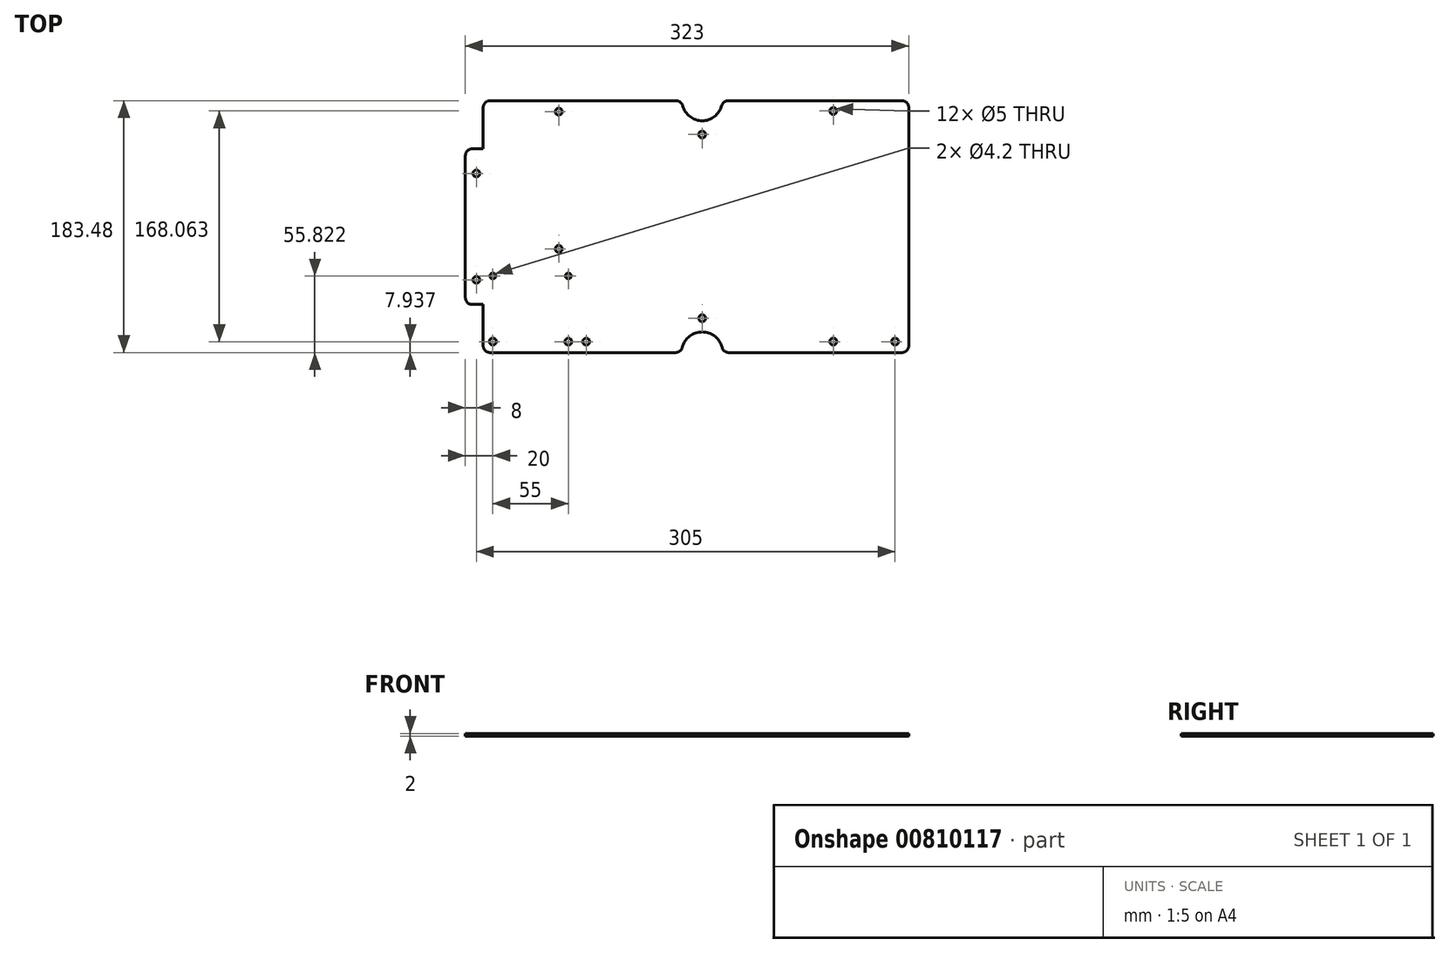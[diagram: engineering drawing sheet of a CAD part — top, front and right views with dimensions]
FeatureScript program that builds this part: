
annotation { "Feature Type Name" : "Feature", "Feature Type Description" : "" }
export const myFeature = defineFeature(function(context is Context, id is Id, definition is map)
    precondition{}
    {
        {
            var Q0;
            Q0=qCreatedBy(makeId("Top.planeOp"),FACE);
            var sketch = newSketch(context, id + "F0", { "sketchPlane" : qUnion([Q0])});
            skLineSegment(sketch, "E0.bottom", {"start": v(-154.5, 90.98) * mm, "end": v(-19, 90.98) * mm});
            skLineSegment(sketch, "E0.top", {"start": v(-154.5, -92.5) * mm, "end": v(-19.36, -92.5) * mm});
            skLineSegment(sketch, "E0.left", {"start": v(-172.5, 50.98) * mm, "end": v(-172.5, -52.5) * mm});
            skLineSegment(sketch, "E0.right", {"start": v(150.5, 85.98) * mm, "end": v(150.5, -87.5) * mm});
            skPoint(sketch, "E0.middle", {"position": v(0, 0) * mm});
            skArc(sketch, "E1.filletArc", {"start": v(145.5, -92.5) * mm, "mid": v(149.04, -91.04) * mm, "end": v(150.5, -87.5) * mm});
            skArc(sketch, "E2.filletArc", {"start": v(150.5, 85.98) * mm, "mid": v(149.04, 89.51) * mm, "end": v(145.5, 90.98) * mm});
            skPoint(sketch, "E3", {"position": v(-104.5, 82.98) * mm});
            skPoint(sketch, "E4.endSnap0", {"position": v(0, 90.98) * mm});
            skPoint(sketch, "E5.endSnap0", {"position": v(-172.5, -0.76) * mm});
            skPoint(sketch, "E6.MirrorP", {"position": v(95.5, 83.5) * mm});
            skPoint(sketch, "E7.MirrorP", {"position": v(162.5, 84.5) * mm});
            skPoint(sketch, "E8.MirrorP", {"position": v(140.5, -84.5) * mm});
            skPoint(sketch, "E9.MirrorP", {"position": v(95.5, -84.5) * mm});
            skPoint(sketch, "E10.MirrorP", {"position": v(-152.5, -84.5) * mm});
            skPoint(sketch, "E11.MirrorP", {"position": v(-97.5, -84.56) * mm});
            skPoint(sketch, "E12", {"position": v(-97.5, -36.68) * mm});
            skPoint(sketch, "E13", {"position": v(-152.5, -36.68) * mm});
            skLineSegment(sketch, "E14.bottom", {"start": v(-167.5, -57.5) * mm, "end": v(-159.5, -57.5) * mm});
            skLineSegment(sketch, "E14.right", {"start": v(-159.5, -57.5) * mm, "end": v(-159.5, -87.5) * mm});
            skPoint(sketch, "E14.left.start.orphan", {"position": v(-172.5, -87.5) * mm});
            skLineSegment(sketch, "E15.bottom", {"start": v(-167.5, 55.98) * mm, "end": v(-159.5, 55.98) * mm});
            skLineSegment(sketch, "E15.right", {"start": v(-159.5, 55.98) * mm, "end": v(-159.5, 85.98) * mm});
            skPoint(sketch, "E16.filletArc.end.orphan", {"position": v(-172.5, 85.98) * mm});
            skPoint(sketch, "E15.top.end.orphan", {"position": v(-145.5, 90.98) * mm});
            skArc(sketch, "E17", {"start": v(-14.17, 87.25) * mm, "mid": v(0, 76.33) * mm, "end": v(14.17, 87.25) * mm});
            skArc(sketch, "E18", {"start": v(14.52, -88.75) * mm, "mid": v(0, -77.5) * mm, "end": v(-14.52, -88.75) * mm});
            skPoint(sketch, "E18.centerSnap0", {"position": v(-7, -92.5) * mm});
            skLineSegment(sketch, "E19.trimOffspring", {"start": v(19, 90.98) * mm, "end": v(145.5, 90.98) * mm});
            skLineSegment(sketch, "E20.trimOffspring", {"start": v(-7, -92.5) * mm, "end": v(0, -92.5) * mm});
            skLineSegment(sketch, "E21.trimOffspring", {"start": v(19.36, -92.5) * mm, "end": v(145.5, -92.5) * mm});
            skPoint(sketch, "E22.visualSharp", {"position": v(14.65, 90.98) * mm});
            skArc(sketch, "E22.filletArc", {"start": v(19, 90.98) * mm, "mid": v(15.95, 89.94) * mm, "end": v(14.17, 87.25) * mm});
            skPoint(sketch, "E23.visualSharp", {"position": v(-14.65, 90.98) * mm});
            skArc(sketch, "E23.filletArc", {"start": v(-14.17, 87.25) * mm, "mid": v(-15.95, 89.94) * mm, "end": v(-19, 90.98) * mm});
            skPoint(sketch, "E24.visualSharp", {"position": v(-15, -92.5) * mm});
            skArc(sketch, "E24.filletArc", {"start": v(-19.36, -92.5) * mm, "mid": v(-16.3, -91.45) * mm, "end": v(-14.52, -88.75) * mm});
            skPoint(sketch, "E25.visualSharp", {"position": v(15, -92.5) * mm});
            skArc(sketch, "E25.filletArc", {"start": v(14.52, -88.75) * mm, "mid": v(16.3, -91.45) * mm, "end": v(19.36, -92.5) * mm});
            skPoint(sketch, "E26.visualSharp", {"position": v(-172.5, -57.5) * mm});
            skArc(sketch, "E26.filletArc", {"start": v(-172.5, -52.5) * mm, "mid": v(-171.04, -56.04) * mm, "end": v(-167.5, -57.5) * mm});
            skPoint(sketch, "E27.visualSharp", {"position": v(-159.5, -92.5) * mm});
            skArc(sketch, "E27.filletArc", {"start": v(-159.5, -87.5) * mm, "mid": v(-158.04, -91.04) * mm, "end": v(-154.5, -92.5) * mm});
            skPoint(sketch, "E28.visualSharp", {"position": v(-172.5, 55.98) * mm});
            skArc(sketch, "E28.filletArc", {"start": v(-167.5, 55.98) * mm, "mid": v(-171.04, 54.51) * mm, "end": v(-172.5, 50.98) * mm});
            skPoint(sketch, "E29.visualSharp", {"position": v(-159.5, 90.98) * mm});
            skArc(sketch, "E29.filletArc", {"start": v(-154.5, 90.98) * mm, "mid": v(-158.04, 89.51) * mm, "end": v(-159.5, 85.98) * mm});
            skPoint(sketch, "E30", {"position": v(-164.5, 37.98) * mm});
            skPoint(sketch, "E31", {"position": v(-164.5, -39.5) * mm});
            skPoint(sketch, "E32", {"position": v(-104.5, -17.02) * mm});
            skPoint(sketch, "E33", {"position": v(-84.5, -84.56) * mm});
            skPoint(sketch, "E34", {"position": v(0, 66.33) * mm});
            skPoint(sketch, "E35", {"position": v(0, -67.5) * mm});
            skSolve(sketch);
        }
        {
            var Q0;
            Q0=makeQuery(id+"F0.imprint","IMPRINT",FACE,{"disambiguationData":[TD([[makeQuery(id+"F0.imprint","IMPRINT",EDGE,{"derivedFrom":sQuery(id+"F0.wireOp",EDGE,"E0.bottom")}),-1.0]])]});
            extrude(context, id + "F1", {"entities" : qUnion([Q0]), "depth" : 2 * mm, "offsetDistance" : 25 * mm});
        }
        {
            var Q0;
            Q0=sQuery(id+"F0.wireOp",VERTEX,"d926d98a-2240-4844-8fc6-3e65a9bc7778");
            var Q1;
            Q1=sQuery(id+"F0.wireOp",VERTEX,"E3");
            var Q2;
            Q2=sQuery(id+"F0.wireOp",VERTEX,"E6.MirrorP");
            var Q3;
            Q3=sQuery(id+"F0.wireOp",VERTEX,"E7.MirrorP");
            var Q4;
            Q4=sQuery(id+"F0.wireOp",VERTEX,"E8.MirrorP");
            var Q5;
            Q5=sQuery(id+"F0.wireOp",VERTEX,"E9.MirrorP");
            var Q6;
            Q6=sQuery(id+"F0.wireOp",VERTEX,"E11.MirrorP");
            var Q7;
            Q7=sQuery(id+"F0.wireOp",VERTEX,"E10.MirrorP");
            var Q8;
            Q8=makeQuery(id+"F1.opExtrude","SWEPT_BODY",BODY,{"disambiguationData":[OSD([sQuery(id+"F0.wireOp",EDGE,"E0.bottom"),sQuery(id+"F0.wireOp",EDGE,"E0.top"),sQuery(id+"F0.wireOp",EDGE,"E0.left"),sQuery(id+"F0.wireOp",EDGE,"E0.right"),sQuery(id+"F0.wireOp",EDGE,"E16.filletArc"),sQuery(id+"F0.wireOp",EDGE,"6a11539f-0376-4b44-992d-93fc49972cab.filletArc"),sQuery(id+"F0.wireOp",EDGE,"E1.filletArc"),sQuery(id+"F0.wireOp",EDGE,"E2.filletArc")])]});
            hole(context, id + "F2", {"style" : HoleStyle.SIMPLE, "endStyle" : HoleEndStyle.BLIND, "oppositeDirection" : true, "standardTappedOrClearance" : lookupTablePath({ "standard" : "ISO", "size" : "5", "type" : "Drilled" }), "standardBlindInLast" : lookupTablePath({ "standard" : "ISO", "size" : "5", "type" : "Drilled" }), "holeDiameter" : 5 * mm, "majorDiameter" : 5 * mm, "holeDepth" : 22.4 * mm, "isTappedThrough" : true, "tappedDepth" : 20 * mm, "tapClearance" : 3, "locations" : qUnion([Q0, Q1, Q2, Q3, Q4, Q5, Q6, Q7]), "scope" : qUnion([Q8])});
        }
        {
            var Q0;
            Q0=sQuery(id+"F0.wireOp",VERTEX,"E12");
            var Q1;
            Q1=sQuery(id+"F0.wireOp",VERTEX,"E13");
            var Q2;
            Q2=makeQuery(id+"F1.opExtrude","SWEPT_BODY",BODY,{"disambiguationData":[OSD([sQuery(id+"F0.wireOp",EDGE,"E0.bottom"),sQuery(id+"F0.wireOp",EDGE,"E0.top"),sQuery(id+"F0.wireOp",EDGE,"E0.left"),sQuery(id+"F0.wireOp",EDGE,"E0.right"),sQuery(id+"F0.wireOp",EDGE,"E16.filletArc"),sQuery(id+"F0.wireOp",EDGE,"6a11539f-0376-4b44-992d-93fc49972cab.filletArc"),sQuery(id+"F0.wireOp",EDGE,"E1.filletArc"),sQuery(id+"F0.wireOp",EDGE,"E2.filletArc")])]});
            hole(context, id + "F3", {"style" : HoleStyle.SIMPLE, "endStyle" : HoleEndStyle.BLIND, "oppositeDirection" : true, "standardTappedOrClearance" : lookupTablePath({ "standard" : "ISO", "engagement" : "75%", "pitch" : "0.8 mm", "size" : "M5", "type" : "Tapped" }), "standardBlindInLast" : lookupTablePath({ "standard" : "ISO", "engagement" : "75%", "pitch" : "0.8 mm", "size" : "M5", "type" : "Tapped" }), "holeDiameter" : 4.2 * mm, "majorDiameter" : 5 * mm, "showTappedDepth" : true, "holeDepth" : 22.4 * mm, "isTappedThrough" : true, "tappedDepth" : 20 * mm, "tapClearance" : 3, "locations" : qUnion([Q0, Q1]), "scope" : qUnion([Q2])});
        }
        {
            var Q0;
            Q0=sQuery(id+"F0.wireOp",VERTEX,"E30");
            var Q1;
            Q1=sQuery(id+"F0.wireOp",VERTEX,"E31");
            var Q2;
            Q2=sQuery(id+"F0.wireOp",VERTEX,"E32");
            var Q3;
            Q3=sQuery(id+"F0.wireOp",VERTEX,"E35");
            var Q4;
            Q4=sQuery(id+"F0.wireOp",VERTEX,"E34");
            var Q5;
            Q5=sQuery(id+"F0.wireOp",VERTEX,"E6.MirrorP");
            var Q6;
            Q6=sQuery(id+"F0.wireOp",VERTEX,"E9.MirrorP");
            var Q7;
            Q7=sQuery(id+"F0.wireOp",VERTEX,"E8.MirrorP");
            var Q8;
            Q8=sQuery(id+"F0.wireOp",VERTEX,"E7.MirrorP");
            var Q9;
            Q9=makeQuery(id+"F1.opExtrude","SWEPT_BODY",BODY,{"disambiguationData":[OSD([sQuery(id+"F0.wireOp",EDGE,"E0.bottom"),sQuery(id+"F0.wireOp",EDGE,"E0.top"),sQuery(id+"F0.wireOp",EDGE,"E0.left"),sQuery(id+"F0.wireOp",EDGE,"E0.right"),sQuery(id+"F0.wireOp",EDGE,"E1.filletArc"),sQuery(id+"F0.wireOp",EDGE,"E2.filletArc"),sQuery(id+"F0.wireOp",EDGE,"E14.bottom"),sQuery(id+"F0.wireOp",EDGE,"E14.right"),sQuery(id+"F0.wireOp",EDGE,"E15.bottom"),sQuery(id+"F0.wireOp",EDGE,"E15.right"),sQuery(id+"F0.wireOp",EDGE,"E17"),sQuery(id+"F0.wireOp",EDGE,"E18"),sQuery(id+"F0.wireOp",EDGE,"E19.trimOffspring"),sQuery(id+"F0.wireOp",EDGE,"E21.trimOffspring"),sQuery(id+"F0.wireOp",EDGE,"E22.filletArc"),sQuery(id+"F0.wireOp",EDGE,"E23.filletArc"),sQuery(id+"F0.wireOp",EDGE,"E24.filletArc"),sQuery(id+"F0.wireOp",EDGE,"E25.filletArc"),sQuery(id+"F0.wireOp",EDGE,"E26.filletArc"),sQuery(id+"F0.wireOp",EDGE,"E27.filletArc"),sQuery(id+"F0.wireOp",EDGE,"E28.filletArc"),sQuery(id+"F0.wireOp",EDGE,"E29.filletArc")])]});
            hole(context, id + "F4", {"style" : HoleStyle.SIMPLE, "endStyle" : HoleEndStyle.BLIND, "oppositeDirection" : true, "holeDiameter" : 5 * mm, "majorDiameter" : 5 * mm, "holeDepth" : 22.4 * mm, "isTappedThrough" : true, "tappedDepth" : 20 * mm, "tapClearance" : 3, "locations" : qUnion([Q0, Q1, Q2, Q3, Q4, Q5, Q6, Q7, Q8]), "scope" : qUnion([Q9])});
        }
        {
            var Q0;
            Q0=sQuery(id+"F0.wireOp",VERTEX,"E33");
            var Q1;
            Q1=makeQuery(id+"F1.opExtrude","SWEPT_BODY",BODY,{"disambiguationData":[OSD([sQuery(id+"F0.wireOp",EDGE,"E0.bottom"),sQuery(id+"F0.wireOp",EDGE,"E0.top"),sQuery(id+"F0.wireOp",EDGE,"E0.left"),sQuery(id+"F0.wireOp",EDGE,"E0.right"),sQuery(id+"F0.wireOp",EDGE,"E1.filletArc"),sQuery(id+"F0.wireOp",EDGE,"E2.filletArc"),sQuery(id+"F0.wireOp",EDGE,"E14.bottom"),sQuery(id+"F0.wireOp",EDGE,"E14.right"),sQuery(id+"F0.wireOp",EDGE,"E15.bottom"),sQuery(id+"F0.wireOp",EDGE,"E15.right"),sQuery(id+"F0.wireOp",EDGE,"E17"),sQuery(id+"F0.wireOp",EDGE,"E18"),sQuery(id+"F0.wireOp",EDGE,"E19.trimOffspring"),sQuery(id+"F0.wireOp",EDGE,"E21.trimOffspring"),sQuery(id+"F0.wireOp",EDGE,"E22.filletArc"),sQuery(id+"F0.wireOp",EDGE,"E23.filletArc"),sQuery(id+"F0.wireOp",EDGE,"E24.filletArc"),sQuery(id+"F0.wireOp",EDGE,"E25.filletArc"),sQuery(id+"F0.wireOp",EDGE,"E26.filletArc"),sQuery(id+"F0.wireOp",EDGE,"E27.filletArc"),sQuery(id+"F0.wireOp",EDGE,"E28.filletArc"),sQuery(id+"F0.wireOp",EDGE,"E29.filletArc")])]});
            hole(context, id + "F5", {"style" : HoleStyle.SIMPLE, "endStyle" : HoleEndStyle.BLIND, "oppositeDirection" : true, "holeDiameter" : 5 * mm, "majorDiameter" : 5 * mm, "holeDepth" : 22.4 * mm, "isTappedThrough" : true, "tappedDepth" : 20 * mm, "tapClearance" : 3, "locations" : qUnion([Q0]), "scope" : qUnion([Q1])});
        }
    });
